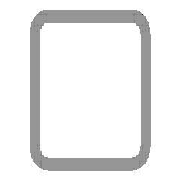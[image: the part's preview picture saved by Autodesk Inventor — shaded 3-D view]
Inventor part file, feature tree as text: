
AUTODESK INVENTOR PART (.ipt)
format: ipt  version: 2025.1 (Build 291241020, 241B)  size: 133,632 bytes
history: native  units: mm (DEFAULTED — no unit token found)
features: other x4, sketch x1, plane x1
ambient origin geometry x8: Origin, YZ Plane, XZ Plane, XY Plane, X Axis, Y Axis, Z Axis, Center Point
bodies: Solid1 (feature_tree), Body (feature_tree)
feature tree (6):
  parser-record x1  (decoder bookkeeping rows leaked as tree rows — omitted from the tree; the rows remain in map.json)
  other  "Driven Length"
  other  "Start Plane"
  other  "End Plane"
  sketch  "Sketch3"  dims[d3=1050.0mm d4=0.0mm d7=4.0mm d9=40.0mm d11=40.0mm d12=2.0mm d13=50.0mm d14=1100.0mm d15=20.0mm d16=20.0mm d17=90.0deg d18=1050.0mm]
  plane  "Work Plane3"
